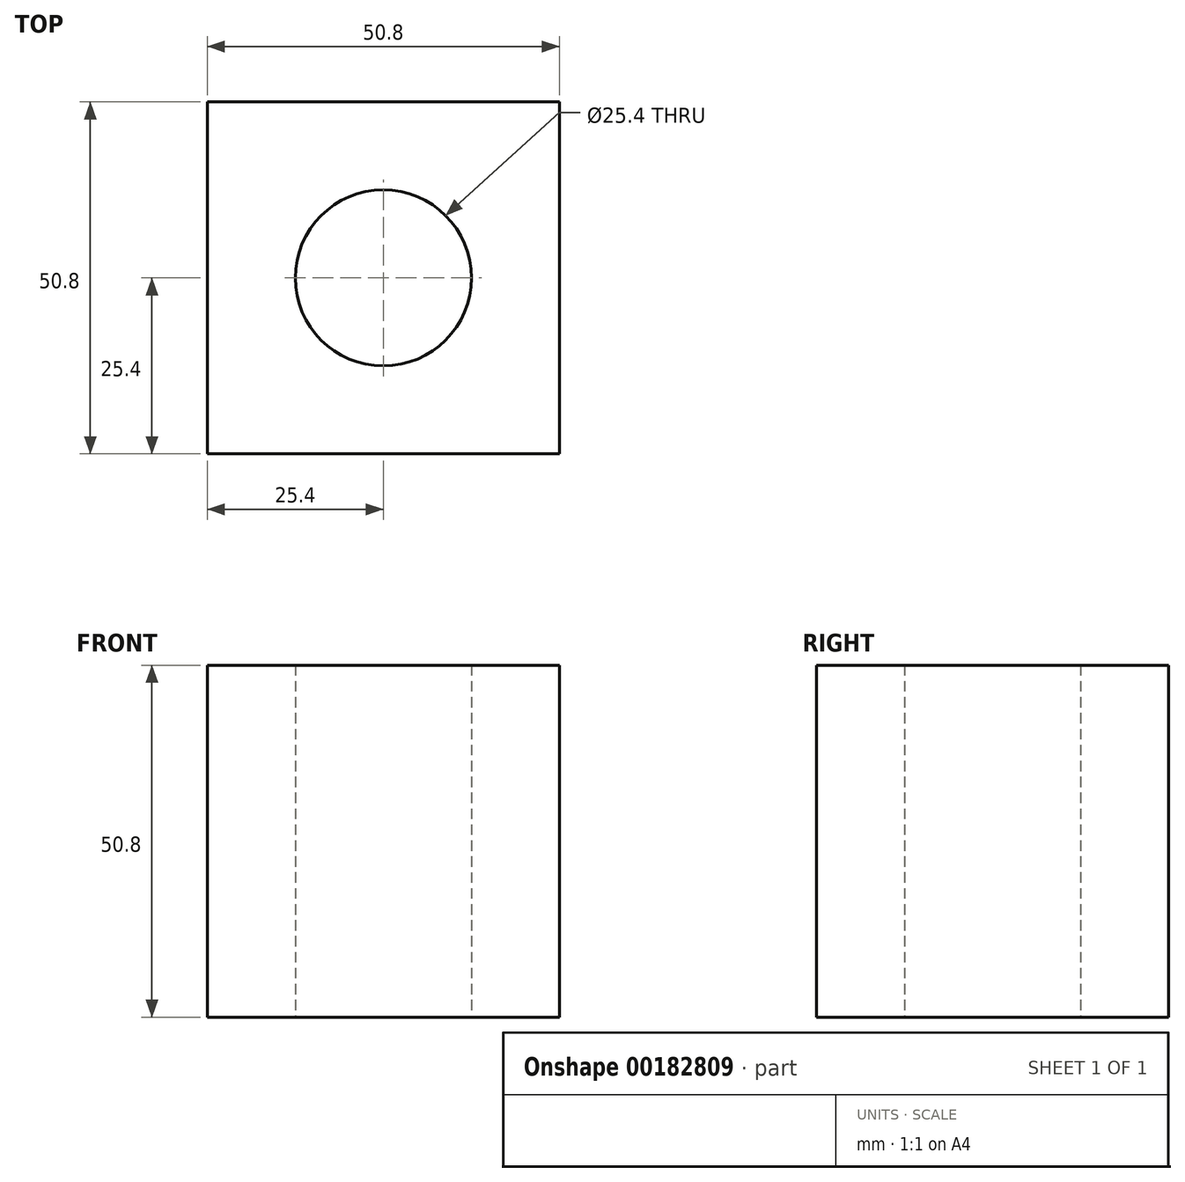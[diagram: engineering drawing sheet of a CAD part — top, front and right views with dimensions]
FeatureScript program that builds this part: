
annotation { "Feature Type Name" : "Feature", "Feature Type Description" : "" }
export const myFeature = defineFeature(function(context is Context, id is Id, definition is map)
    precondition{}
    {
        {
            var Q0;
            Q0=qCreatedBy(makeId("Top.planeOp"),FACE);
            var sketch = newSketch(context, id + "F0", { "sketchPlane" : qUnion([Q0])});
            skLineSegment(sketch, "E0.bottom", {"start": v(-25.4, 25.4) * mm, "end": v(25.4, 25.4) * mm});
            skLineSegment(sketch, "E0.top", {"start": v(-25.4, -25.4) * mm, "end": v(25.4, -25.4) * mm});
            skLineSegment(sketch, "E0.left", {"start": v(-25.4, 25.4) * mm, "end": v(-25.4, -25.4) * mm});
            skLineSegment(sketch, "E0.right", {"start": v(25.4, 25.4) * mm, "end": v(25.4, -25.4) * mm});
            skPoint(sketch, "E0.middle", {"position": v(0, 0) * mm});
            skCircle(sketch, "E1", {"center": v(0, 0) * mm, "radius": 12.7 * mm});
            skSolve(sketch);
        }
        {
            var Q0;
            Q0 = qSketchRegion(id + "F0", true);
            extrude(context, id + "F1", {"entities" : qUnion([Q0]), "depth" : 50.8 * mm});
        }
    });
